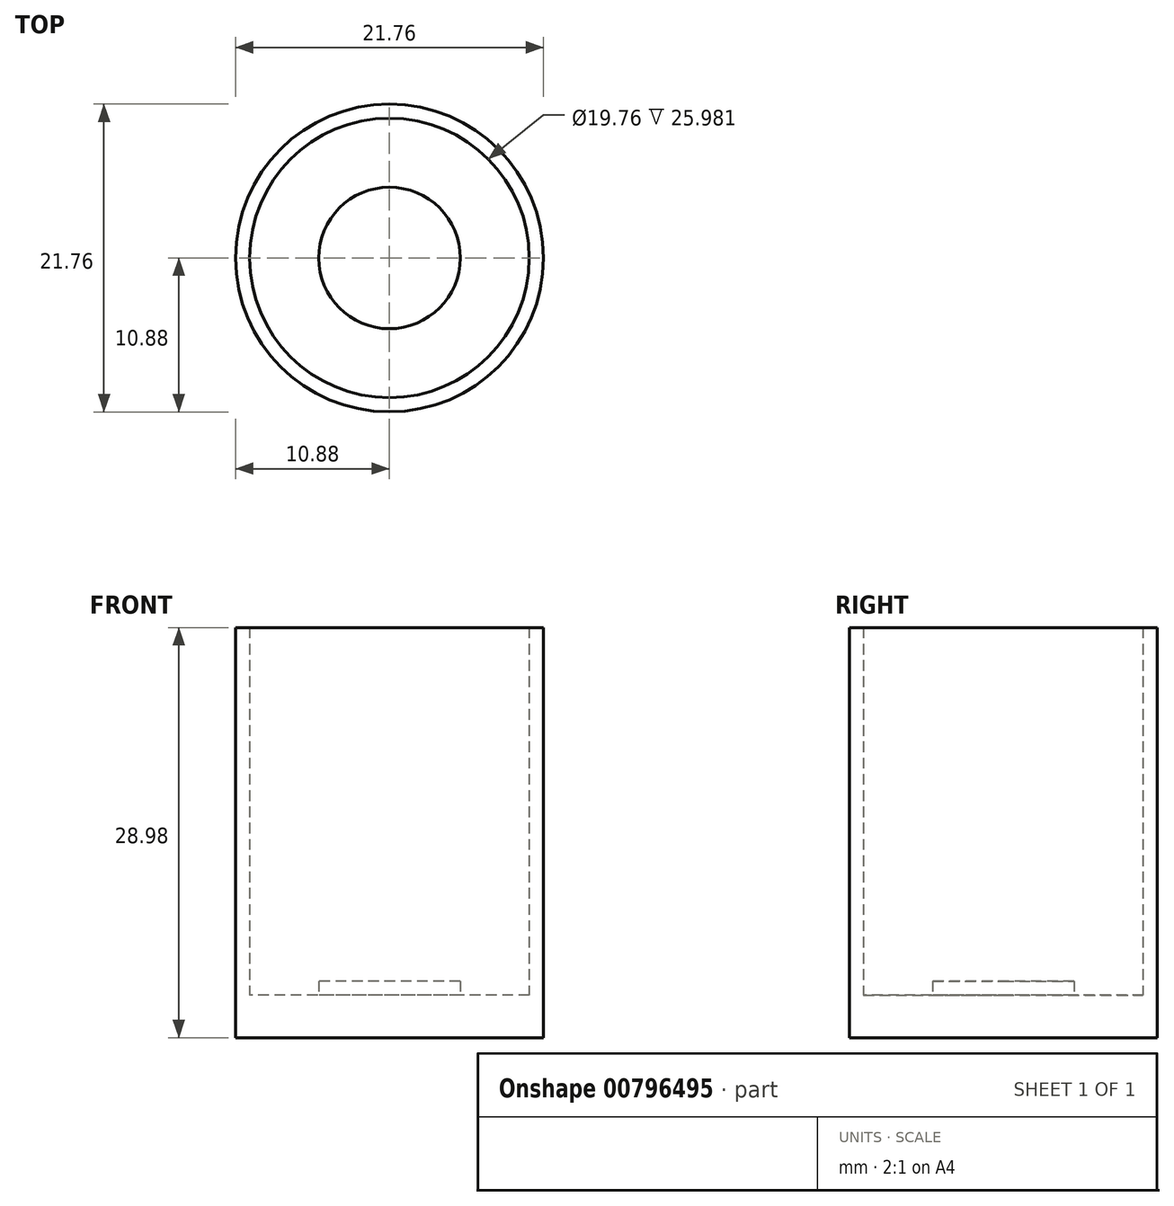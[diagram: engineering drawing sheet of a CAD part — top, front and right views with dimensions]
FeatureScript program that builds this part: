
annotation { "Feature Type Name" : "Feature", "Feature Type Description" : "" }
export const myFeature = defineFeature(function(context is Context, id is Id, definition is map)
    precondition{}
    {
        {
            var Q0;
            Q0=qCreatedBy(makeId("Top.planeOp"),FACE);
            var sketch = newSketch(context, id + "F0", { "sketchPlane" : qUnion([Q0])});
            skCircle(sketch, "E0", {"center": v(0, 0) * mm, "radius": 5.4 * mm});
            skCircle(sketch, "E1", {"center": v(0, 0) * mm, "radius": 6.5 * mm});
            skCircle(sketch, "E2.0", {"center": v(0, 0) * mm, "radius": 5 * mm});
            skCircle(sketch, "E3.0", {"center": v(0, 0) * mm, "radius": 9.88 * mm});
            skCircle(sketch, "E4.0", {"center": v(0, 0) * mm, "radius": 10.88 * mm});
            skSolve(sketch);
        }
        {
            var Q0;
            Q0=makeQuery(id+"F0.imprint","IMPRINT",FACE,{"disambiguationData":[TD([[makeQuery(id+"F0.imprint","IMPRINT",EDGE,{"derivedFrom":sQuery(id+"F0.wireOp",EDGE,"E3.0")}),-1.0]])]});
            var Q1;
            Q1=makeQuery(id+"F0.imprint","IMPRINT",FACE,{"disambiguationData":[TD([[makeQuery(id+"F0.imprint","IMPRINT",EDGE,{"derivedFrom":sQuery(id+"F0.wireOp",EDGE,"E1")}),-1.0]])]});
            var Q2;
            Q2=makeQuery(id+"F0.imprint","IMPRINT",FACE,{"disambiguationData":[TD([[makeQuery(id+"F0.imprint","IMPRINT",EDGE,{"derivedFrom":sQuery(id+"F0.wireOp",EDGE,"E0")}),-1.0]])]});
            var Q3;
            Q3=makeQuery(id+"F0.imprint","IMPRINT",FACE,{"disambiguationData":[TD([[makeQuery(id+"F0.imprint","IMPRINT",EDGE,{"derivedFrom":sQuery(id+"F0.wireOp",EDGE,"E0")}),1.0]])]});
            var Q4;
            Q4=makeQuery(id+"F0.imprint","IMPRINT",FACE,{"disambiguationData":[TD([[makeQuery(id+"F0.imprint","IMPRINT",EDGE,{"derivedFrom":sQuery(id+"F0.wireOp",EDGE,"E2.0")}),1.0]])]});
            extrude(context, id + "F1", {"entities" : qUnion([Q0, Q1, Q2, Q3, Q4]), "depth" : 3 * mm, "offsetDistance" : 25.4 * mm});
        }
        {
            var Q0;
            Q0=makeQuery(id+"F0.imprint","IMPRINT",FACE,{"disambiguationData":[TD([[makeQuery(id+"F0.imprint","IMPRINT",EDGE,{"derivedFrom":sQuery(id+"F0.wireOp",EDGE,"E3.0")}),-1.0]])]});
            extrude(context, id + "F2", {"entities" : qUnion([Q0]), "operationType" : NewBodyOperationType.ADD, "depth" : 28.98 * mm, "offsetDistance" : 25.4 * mm});
        }
        {
            var Q0;
            Q0=makeQuery(id+"F0.imprint","IMPRINT",FACE,{"disambiguationData":[TD([[makeQuery(id+"F0.imprint","IMPRINT",EDGE,{"derivedFrom":sQuery(id+"F0.wireOp",EDGE,"E2.0")}),1.0]])]});
            extrude(context, id + "F3", {"entities" : qUnion([Q0]), "operationType" : NewBodyOperationType.ADD, "depth" : 4 * mm, "offsetDistance" : 25.4 * mm});
        }
    });
